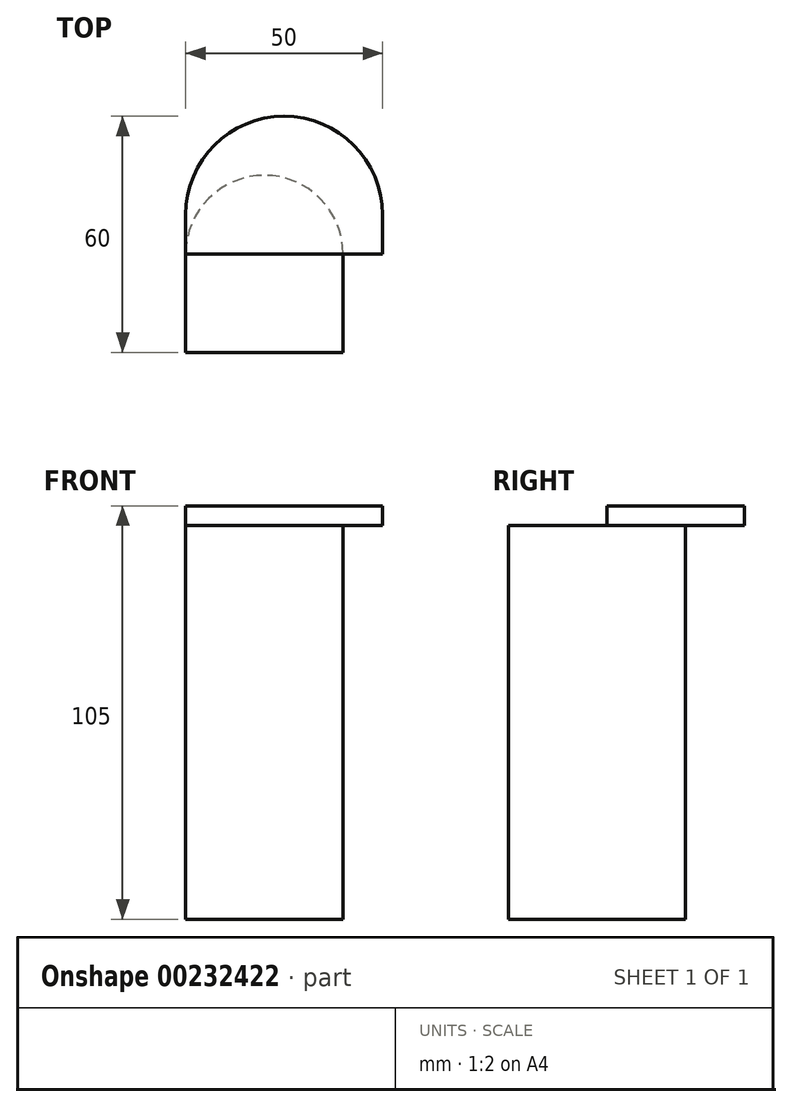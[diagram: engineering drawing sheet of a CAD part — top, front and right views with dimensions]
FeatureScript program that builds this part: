
annotation { "Feature Type Name" : "Feature", "Feature Type Description" : "" }
export const myFeature = defineFeature(function(context is Context, id is Id, definition is map)
    precondition{}
    {
        {
            var Q0;
            Q0=qCreatedBy(makeId("Top.planeOp"),FACE);
            var sketch = newSketch(context, id + "F0", { "sketchPlane" : qUnion([Q0])});
            skCircle(sketch, "E0", {"center": v(0, 0) * mm, "radius": 20 * mm});
            skLineSegment(sketch, "E1.bottom", {"start": v(20, 0) * mm, "end": v(-20, 0) * mm});
            skLineSegment(sketch, "E1.top", {"start": v(20, -25) * mm, "end": v(-20, -25) * mm});
            skLineSegment(sketch, "E1.left", {"start": v(20, 0) * mm, "end": v(20, -25) * mm});
            skLineSegment(sketch, "E1.right", {"start": v(-20, 0) * mm, "end": v(-20, -25) * mm});
            skSolve(sketch);
        }
        {
            var Q0;
            Q0 = qSketchRegion(id + "F0", true);
            extrude(context, id + "F1", {"entities" : qUnion([Q0]), "depth" : 100 * mm});
        }
        {
            var Q0;
            Q0=makeQuery(id+"F1.opExtrude","CAP_FACE",FACE,{"disambiguationData":[OSD([sQuery(id+"F0.wireOp",EDGE,"E0")])],"isStart":false});
            var sketch = newSketch(context, id + "F2", { "sketchPlane" : qUnion([Q0])});
            skLineSegment(sketch, "E2.bottom", {"start": v(-20, 0) * mm, "end": v(30, 0) * mm});
            skLineSegment(sketch, "E2.left", {"start": v(-20, 0) * mm, "end": v(-20, 10) * mm});
            skLineSegment(sketch, "E2.right", {"start": v(30, 0) * mm, "end": v(30, 10) * mm});
            skArc(sketch, "E3.trimOffspring", {"start": v(30, 10) * mm, "mid": v(5, 35) * mm, "end": v(-20, 10) * mm});
            skSolve(sketch);
        }
        {
            var Q0;
            Q0 = qSketchRegion(id + "F2", true);
            extrude(context, id + "F3", {"entities" : qUnion([Q0]), "operationType" : NewBodyOperationType.ADD, "depth" : 5 * mm});
        }
    });
